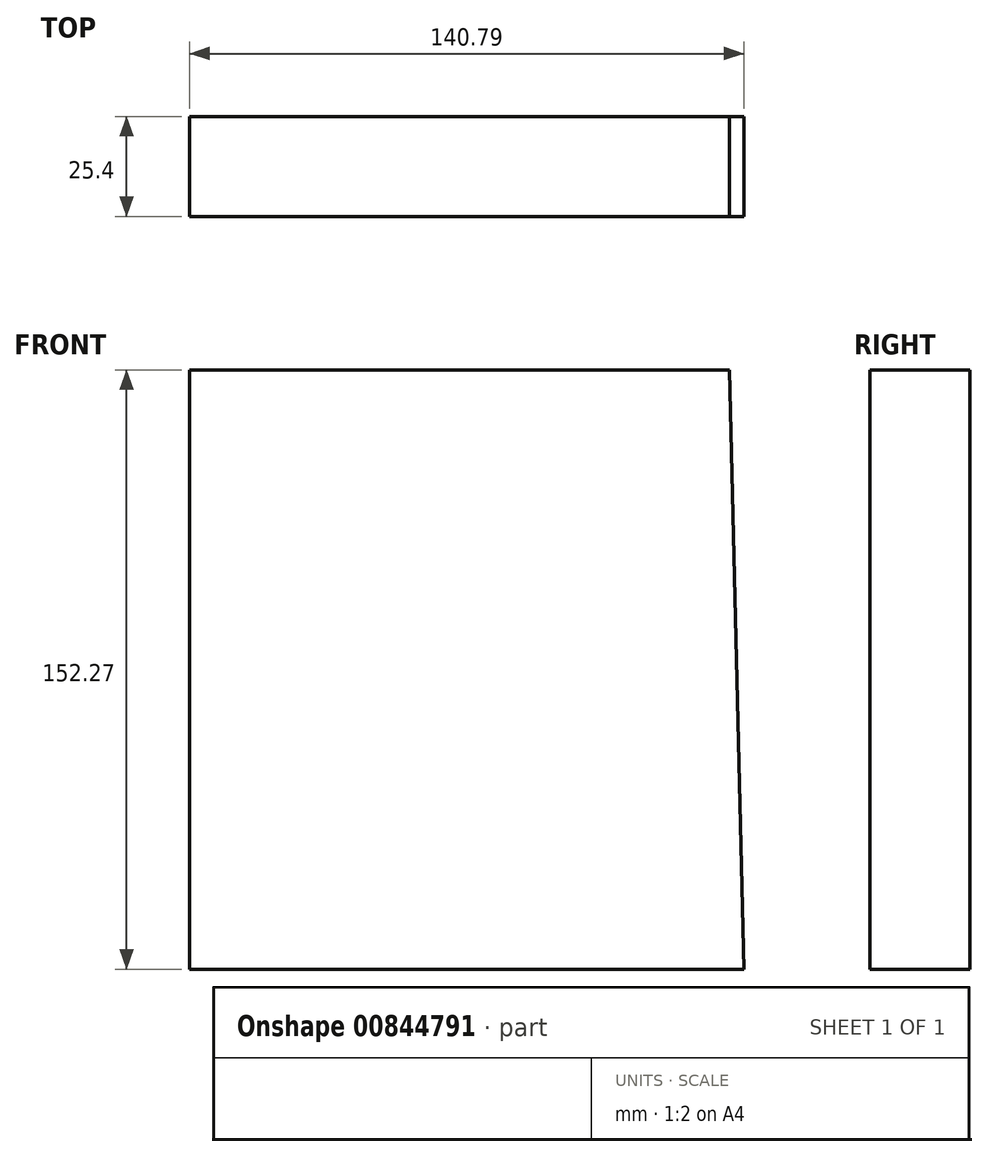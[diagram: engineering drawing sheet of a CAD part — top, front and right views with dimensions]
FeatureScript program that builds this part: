
annotation { "Feature Type Name" : "Feature", "Feature Type Description" : "" }
export const myFeature = defineFeature(function(context is Context, id is Id, definition is map)
    precondition{}
    {
        {
            var Q0;
            Q0=qCreatedBy(makeId("Front.planeOp"),FACE);
            var sketch = newSketch(context, id + "F0", { "sketchPlane" : qUnion([Q0])});
            skPoint(sketch, "E0.0", {"position": v(0, 0) * mm});
            skLineSegment(sketch, "E1", {"start": v(72.1, 74.55) * mm, "end": v(-65.01, 74.55) * mm});
            skLineSegment(sketch, "E2", {"start": v(-65.01, 74.55) * mm, "end": v(-65.01, -77.72) * mm});
            skLineSegment(sketch, "E3", {"start": v(-65.01, -77.72) * mm, "end": v(75.78, -77.72) * mm});
            skLineSegment(sketch, "E4", {"start": v(75.78, -77.72) * mm, "end": v(72.1, 74.55) * mm});
            skSolve(sketch);
        }
        {
            var Q0;
            Q0 = qSketchRegion(id + "F0", true);
            extrude(context, id + "F1", {"entities" : qUnion([Q0]), "depth" : 25.4 * mm, "offsetDistance" : 25.4 * mm});
        }
        {
            var Q0;
            Q0=qCreatedBy(makeId("Right.planeOp"),FACE);
            var sketch = newSketch(context, id + "F2", { "sketchPlane" : qUnion([Q0])});
            skLineSegment(sketch, "E5", {"start": v(-63.24, 64.27) * mm, "end": v(62.07, 64.27) * mm});
            skLineSegment(sketch, "E6", {"start": v(62.07, 64.27) * mm, "end": v(52.16, 18.78) * mm});
            skLineSegment(sketch, "E7", {"start": v(-57.8, 17.16) * mm, "end": v(-63.24, 64.27) * mm});
            skLineSegment(sketch, "E8", {"start": v(52.16, 18.78) * mm, "end": v(-57.8, 17.16) * mm});
            skSolve(sketch);
        }
        {
            var Q0;
            Q0 = qBodyType(qCreatedBy(id + "F2" ,EDGE), BodyType.WIRE);
            var Q1;
            Q1=sQuery(id+"F2.wireOp",EDGE,"E5");
            extrude(context, id + "F3", {"bodyType" : ToolBodyType.SURFACE, "surfaceEntities" : qUnion([Q0, Q1]), "depth" : 25.4 * mm, "offsetDistance" : 25.4 * mm});
        }
    });
